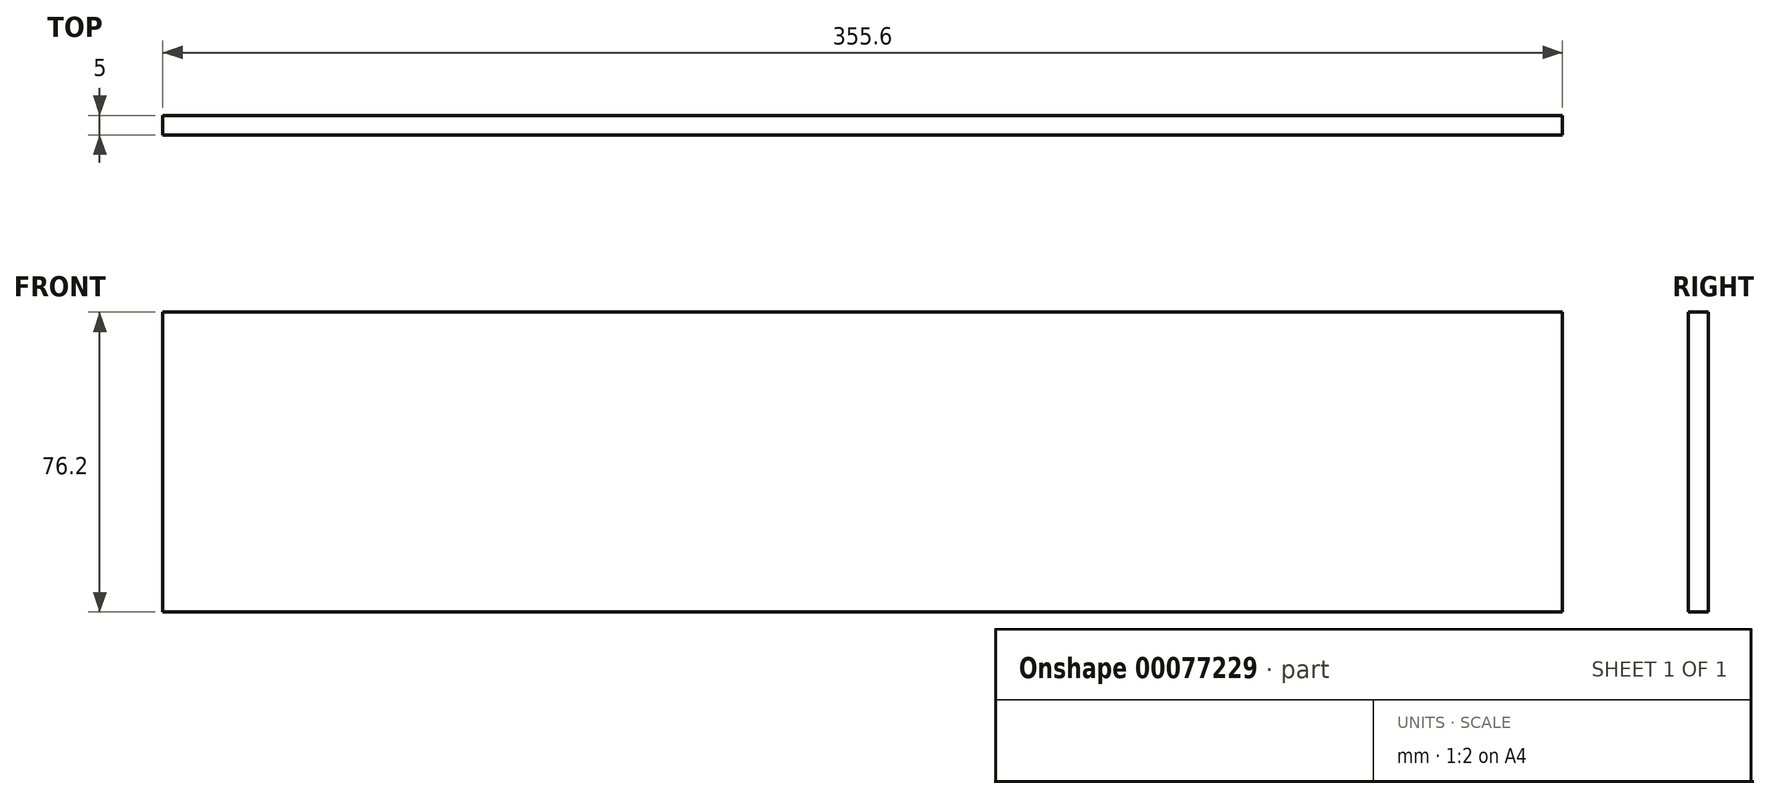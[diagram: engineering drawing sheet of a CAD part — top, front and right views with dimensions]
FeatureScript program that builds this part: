
annotation { "Feature Type Name" : "Feature", "Feature Type Description" : "" }
export const myFeature = defineFeature(function(context is Context, id is Id, definition is map)
    precondition{}
    {
        {
            var Q0;
            Q0=qCreatedBy(makeId("Front.planeOp"),FACE);
            var sketch = newSketch(context, id + "F0", { "sketchPlane" : qUnion([Q0])});
            skLineSegment(sketch, "E0.bottom", {"start": v(-169.9, -21.45) * mm, "end": v(185.7, -21.45) * mm});
            skLineSegment(sketch, "E0.top", {"start": v(-169.9, -97.65) * mm, "end": v(185.7, -97.65) * mm});
            skLineSegment(sketch, "E0.left", {"start": v(-169.9, -21.45) * mm, "end": v(-169.9, -97.65) * mm});
            skLineSegment(sketch, "E0.right", {"start": v(185.7, -21.45) * mm, "end": v(185.7, -97.65) * mm});
            skSolve(sketch);
        }
        {
            var Q0;
            Q0=makeQuery(id+"F0.imprint","IMPRINT",FACE,{"disambiguationData":[TD([[makeQuery(id+"F0.imprint","IMPRINT",EDGE,{"derivedFrom":sQuery(id+"F0.wireOp",EDGE,"E0.bottom")}),-1.0]])]});
            extrude(context, id + "F1", {"entities" : qUnion([Q0]), "depth" : 5 * mm});
        }
    });
